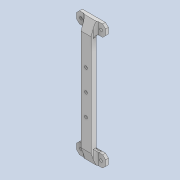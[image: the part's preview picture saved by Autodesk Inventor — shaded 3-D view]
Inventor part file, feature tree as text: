
AUTODESK INVENTOR PART (.ipt)
format: ipt  version: 2023 (Build 270158000, 158)  size: 183,808 bytes
history: native  units: mm
features: other x6, extrude x3, chamfer x3, sketch x3, projected_geometry x3, fillet x2, reference x2
ambient origin geometry x8: Origin, YZ Plane, XZ Plane, XY Plane, X Axis, Y Axis, Z Axis, Center Point
bodies: Solid1 (feature_tree)
feature tree (22):
  extrude  "Extrusion1"  Depth=2.0mm
  extrude  "Extrusion2"  Depth=2.0mm
  fillet  "Fillet1"  Radius=2.0mm
  fillet  "Fillet2"  Radius=7.0mm
  chamfer  "Chamfer1"  Distance=3.5mm
  chamfer  "Chamfer2"  Distance=2.0mm
  chamfer  "Chamfer3"  Distance=2.0mm
  extrude  "Extrusion3"  Depth=2.0mm TaperAngle=45.0deg
  sketch  "Sketch1"  dims[d0=2.0mm d1=2.0mm]
  reference  "Reference1"
  reference  "Reference2"
  sketch  "Sketch2"  dims[d2=2.0mm d3=2.0mm d4=2.0mm d5=0.0mm d6=7.0mm]
  projected_geometry  "Projected Loop1"
  projected_geometry  "Projected Loop2"
  sketch  "Sketch3"  dims[d7=87.0mm d8=3.5mm d9=0.0mm d10=2.0mm d11=2.0mm d12=2.0mm d13=2.0mm d14=45.0deg d15=3.0mm d16=2.0mm d17=12.217305mm d18=3.0mm d19=2.0mm d20=12.217305mm d21=2.0mm d22=15.0mm d23=2.0mm d24=15.0mm d25=2.0mm d26=3.5mm d27=0.0mm]
  projected_geometry  "Projected Loop3"
  parser-record x1  (decoder bookkeeping rows leaked as tree rows — omitted from the tree; the rows remain in map.json)
  other  "body_8d_1.iam"
  other  "leg_1_2d_MIR:1"
  other  "leg_holder_2_MIR:1"
  other  "leg_2d_1:1"
  other  "leg_holder_2:1"
note: 1 file-system path scrubbed to <path> (originals preserved in map.json)
